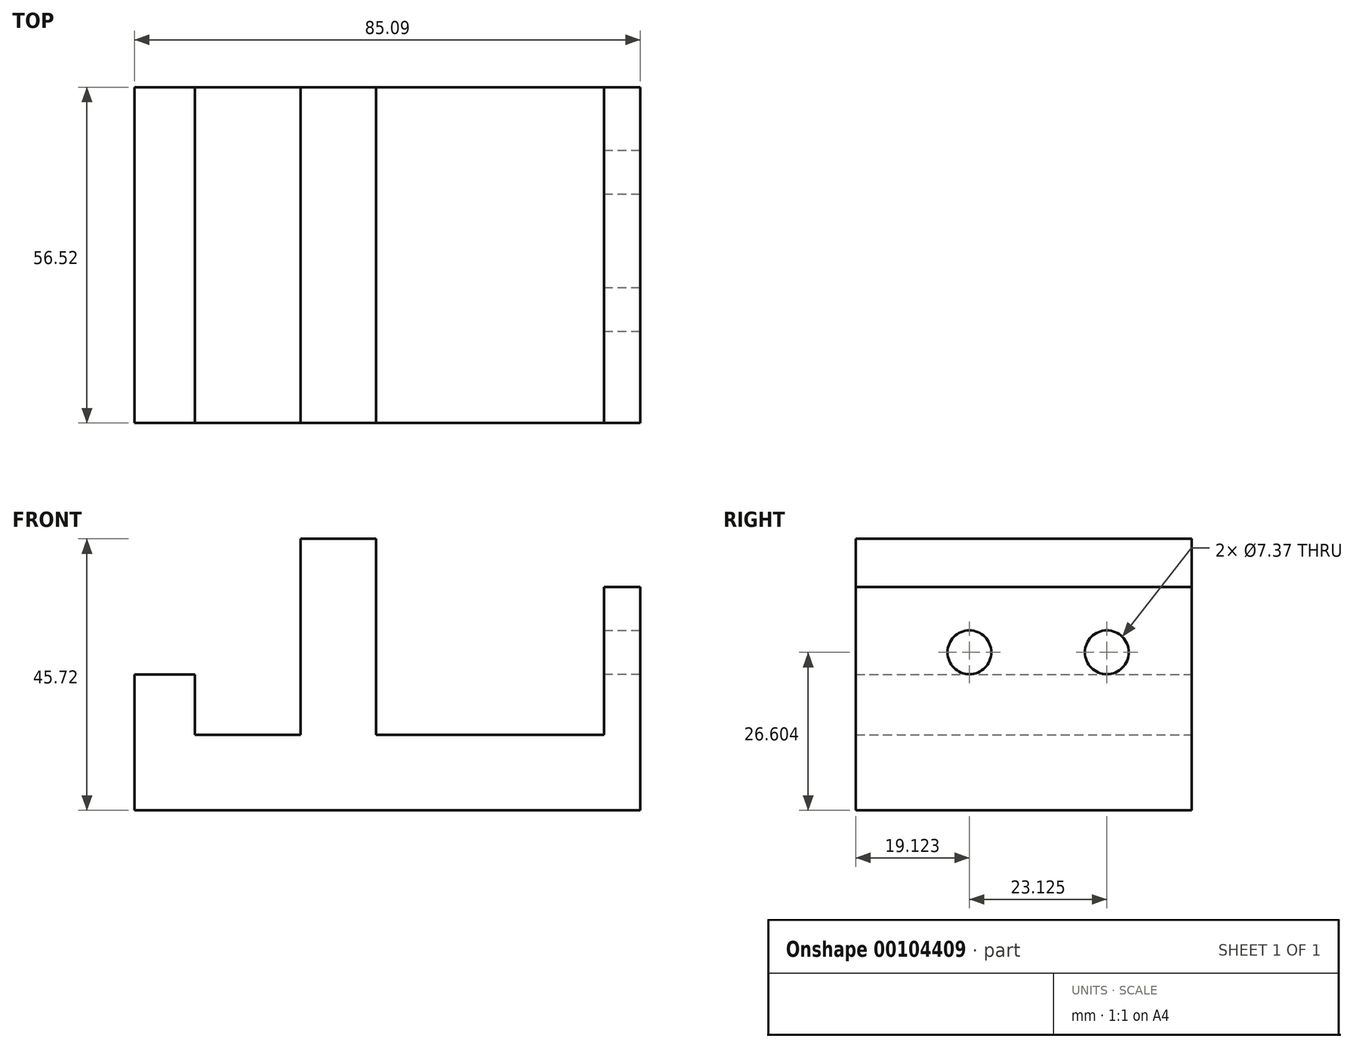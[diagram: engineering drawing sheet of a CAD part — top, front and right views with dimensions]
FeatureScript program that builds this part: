
annotation { "Feature Type Name" : "Feature", "Feature Type Description" : "" }
export const myFeature = defineFeature(function(context is Context, id is Id, definition is map)
    precondition{}
    {
        {
            var Q0;
            Q0=qCreatedBy(makeId("Front.planeOp"),FACE);
            var sketch = newSketch(context, id + "F0", { "sketchPlane" : qUnion([Q0])});
            skLineSegment(sketch, "E0.bottom", {"start": v(10.16, 0) * mm, "end": v(27.94, 0) * mm});
            skLineSegment(sketch, "E0.top", {"start": v(0, -12.7) * mm, "end": v(85.1, -12.7) * mm});
            skLineSegment(sketch, "E0.left", {"start": v(0, 0) * mm, "end": v(0, -12.7) * mm});
            skLineSegment(sketch, "E0.right", {"start": v(85.1, 0) * mm, "end": v(85.1, -12.7) * mm});
            skLineSegment(sketch, "E1.top", {"start": v(27.94, 33.02) * mm, "end": v(40.64, 33.02) * mm});
            skLineSegment(sketch, "E1.left", {"start": v(27.94, 0) * mm, "end": v(27.94, 33.02) * mm});
            skLineSegment(sketch, "E1.right", {"start": v(40.64, 0) * mm, "end": v(40.64, 33.02) * mm});
            skLineSegment(sketch, "E2.top", {"start": v(0, 10.16) * mm, "end": v(10.16, 10.16) * mm});
            skLineSegment(sketch, "E2.left", {"start": v(0, 0) * mm, "end": v(0, 10.16) * mm});
            skLineSegment(sketch, "E2.right", {"start": v(10.16, 0) * mm, "end": v(10.16, 10.16) * mm});
            skLineSegment(sketch, "E3.trimOffspring", {"start": v(40.64, 0) * mm, "end": v(78.96, 0) * mm});
            skLineSegment(sketch, "E4.top", {"start": v(85.1, 24.9) * mm, "end": v(78.96, 24.9) * mm});
            skLineSegment(sketch, "E4.left", {"start": v(85.1, 0) * mm, "end": v(85.1, 24.9) * mm});
            skLineSegment(sketch, "E4.right", {"start": v(78.96, 0) * mm, "end": v(78.96, 24.9) * mm});
            skSolve(sketch);
        }
        {
            var Q0;
            Q0=makeQuery(id+"F0.imprint","IMPRINT",FACE,{"disambiguationData":[TD([[makeQuery(id+"F0.imprint","IMPRINT",EDGE,{"derivedFrom":sQuery(id+"F0.wireOp",EDGE,"E0.bottom")}),-1.0]])]});
            extrude(context, id + "F1", {"entities" : qUnion([Q0]), "depth" : 56.52 * mm});
        }
        {
            var Q0;
            Q0=makeQuery(id+"F1.opExtrude","SWEPT_FACE",FACE,{"disambiguationData":[OSD([sQuery(id+"F0.wireOp",EDGE,"E0.right"),sQuery(id+"F0.wireOp",EDGE,"E4.left")])]});
            var sketch = newSketch(context, id + "F2", { "sketchPlane" : qUnion([Q0])});
            skCircle(sketch, "E5", {"center": v(-37.4, 13.9) * mm, "radius": 3.68 * mm});
            skCircle(sketch, "E6", {"center": v(-14.27, 13.9) * mm, "radius": 3.68 * mm});
            skSolve(sketch);
        }
        {
            var Q0;
            Q0=sQuery(id+"F2.wireOp",VERTEX,"E5.center");
            var Q1;
            Q1=makeQuery(id+"F1.opExtrude","SWEPT_BODY",BODY,{"disambiguationData":[OSD([sQuery(id+"F0.wireOp",EDGE,"E0.bottom"),sQuery(id+"F0.wireOp",EDGE,"E0.top"),sQuery(id+"F0.wireOp",EDGE,"E0.left"),sQuery(id+"F0.wireOp",EDGE,"E0.right"),sQuery(id+"F0.wireOp",EDGE,"E1.top"),sQuery(id+"F0.wireOp",EDGE,"E1.left"),sQuery(id+"F0.wireOp",EDGE,"E1.right"),sQuery(id+"F0.wireOp",EDGE,"E2.top"),sQuery(id+"F0.wireOp",EDGE,"E2.left"),sQuery(id+"F0.wireOp",EDGE,"E2.right"),sQuery(id+"F0.wireOp",EDGE,"E3.trimOffspring"),sQuery(id+"F0.wireOp",EDGE,"E4.top"),sQuery(id+"F0.wireOp",EDGE,"E4.left"),sQuery(id+"F0.wireOp",EDGE,"E4.right")])]});
            hole(context, id + "F3", {"style" : HoleStyle.SIMPLE, "endStyle" : HoleEndStyle.BLIND, "holeDiameter" : 7.37 * mm, "holeDepth" : 10.16 * mm, "locations" : qUnion([Q0]), "scope" : qUnion([Q1])});
        }
        {
            var Q0;
            Q0=sQuery(id+"F2.wireOp",VERTEX,"E6.center");
            var Q1;
            Q1=makeQuery(id+"F1.opExtrude","SWEPT_BODY",BODY,{"disambiguationData":[OSD([sQuery(id+"F0.wireOp",EDGE,"E0.bottom"),sQuery(id+"F0.wireOp",EDGE,"E0.top"),sQuery(id+"F0.wireOp",EDGE,"E0.left"),sQuery(id+"F0.wireOp",EDGE,"E0.right"),sQuery(id+"F0.wireOp",EDGE,"E1.top"),sQuery(id+"F0.wireOp",EDGE,"E1.left"),sQuery(id+"F0.wireOp",EDGE,"E1.right"),sQuery(id+"F0.wireOp",EDGE,"E2.top"),sQuery(id+"F0.wireOp",EDGE,"E2.left"),sQuery(id+"F0.wireOp",EDGE,"E2.right"),sQuery(id+"F0.wireOp",EDGE,"E3.trimOffspring"),sQuery(id+"F0.wireOp",EDGE,"E4.top"),sQuery(id+"F0.wireOp",EDGE,"E4.left"),sQuery(id+"F0.wireOp",EDGE,"E4.right")])]});
            hole(context, id + "F4", {"style" : HoleStyle.SIMPLE, "endStyle" : HoleEndStyle.BLIND, "holeDiameter" : 7.37 * mm, "holeDepth" : 10.16 * mm, "locations" : qUnion([Q0]), "scope" : qUnion([Q1])});
        }
    });
